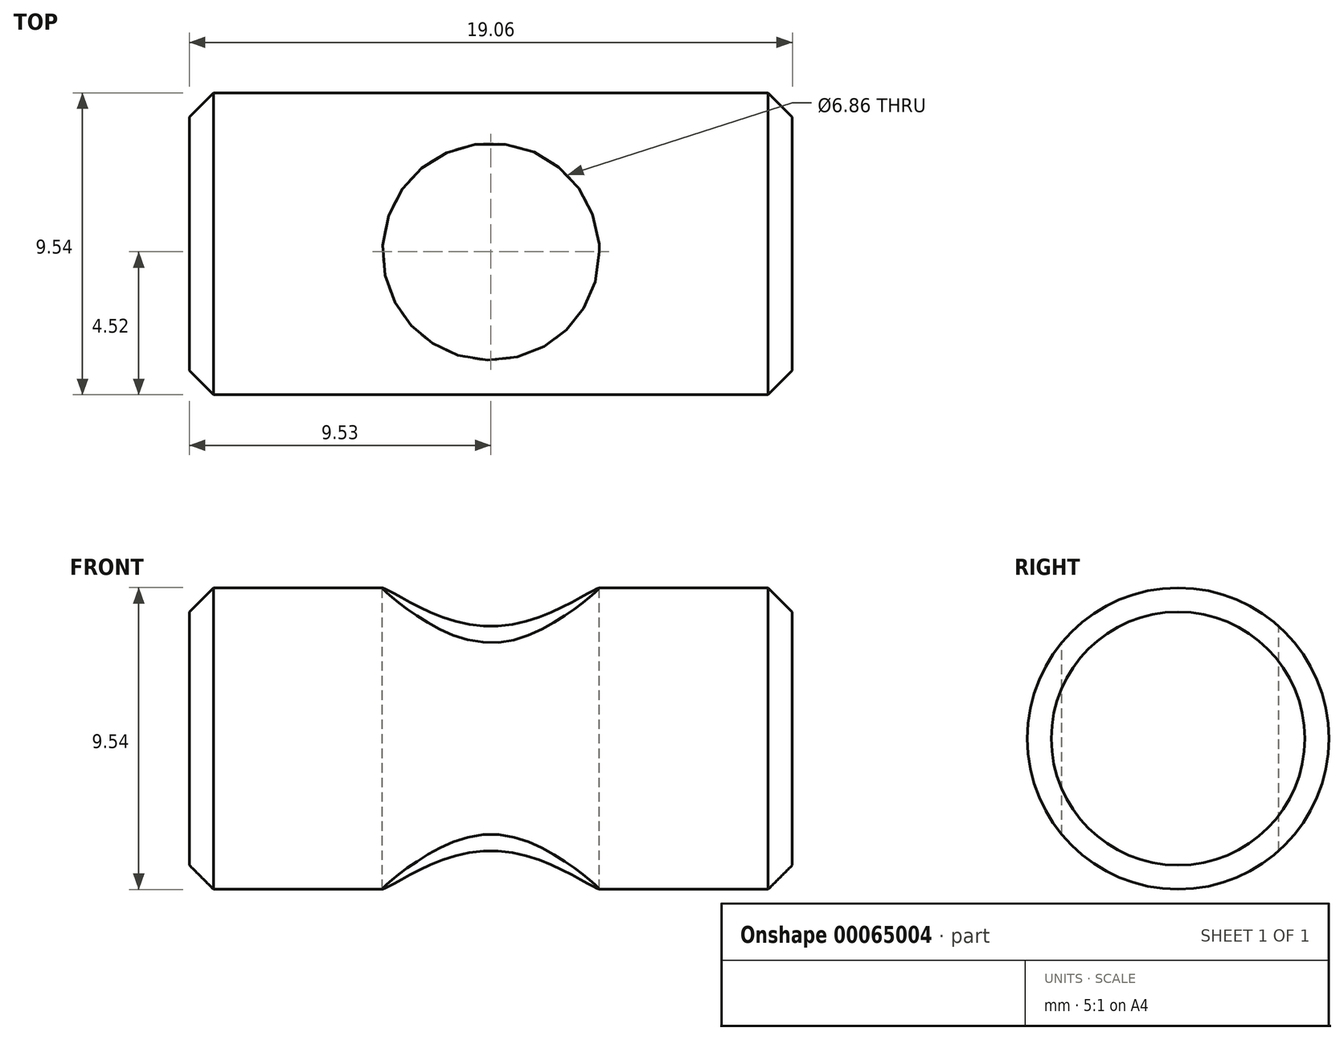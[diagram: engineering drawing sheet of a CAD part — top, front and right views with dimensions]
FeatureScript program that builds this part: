
annotation { "Feature Type Name" : "Feature", "Feature Type Description" : "" }
export const myFeature = defineFeature(function(context is Context, id is Id, definition is map)
    precondition{}
    {
        {
            var Q0;
            Q0=qCreatedBy(makeId("Right.planeOp"),FACE);
            var sketch = newSketch(context, id + "F0", { "sketchPlane" : qUnion([Q0])});
            skCircle(sketch, "E0", {"center": v(0, 0) * mm, "radius": 4.77 * mm});
            skSolve(sketch);
        }
        {
            var Q0;
            Q0 = qSketchRegion(id + "F0", true);
            extrude(context, id + "F1", {"entities" : qUnion([Q0]), "endBound" : BoundingType.SYMMETRIC, "depth" : 19.05 * mm});
        }
        {
            var Q0;
            Q0=makeQuery(id+"F1.opExtrude","SWEPT_FACE",FACE,{"disambiguationData":[OSD([sQuery(id+"F0.wireOp",EDGE,"E0")])]});
            chamfer(context, id + "F2", {"entities" : qUnion([Q0]), "width" : 0.76 * mm, "tangentPropagation" : true});
        }
        {
            var Q0;
            Q0=qCreatedBy(makeId("Top.planeOp"),FACE);
            var sketch = newSketch(context, id + "F3", { "sketchPlane" : qUnion([Q0])});
            skCircle(sketch, "E1", {"center": v(0, -0.25) * mm, "radius": 3.43 * mm});
            skSolve(sketch);
        }
        {
            var Q0;
            Q0 = qSketchRegion(id + "F3", true);
            extrude(context, id + "F4", {"entities" : qUnion([Q0]), "operationType" : NewBodyOperationType.REMOVE, "endBound" : BoundingType.SYMMETRIC, "oppositeDirection" : true, "depth" : 25.4 * mm});
        }
    });
